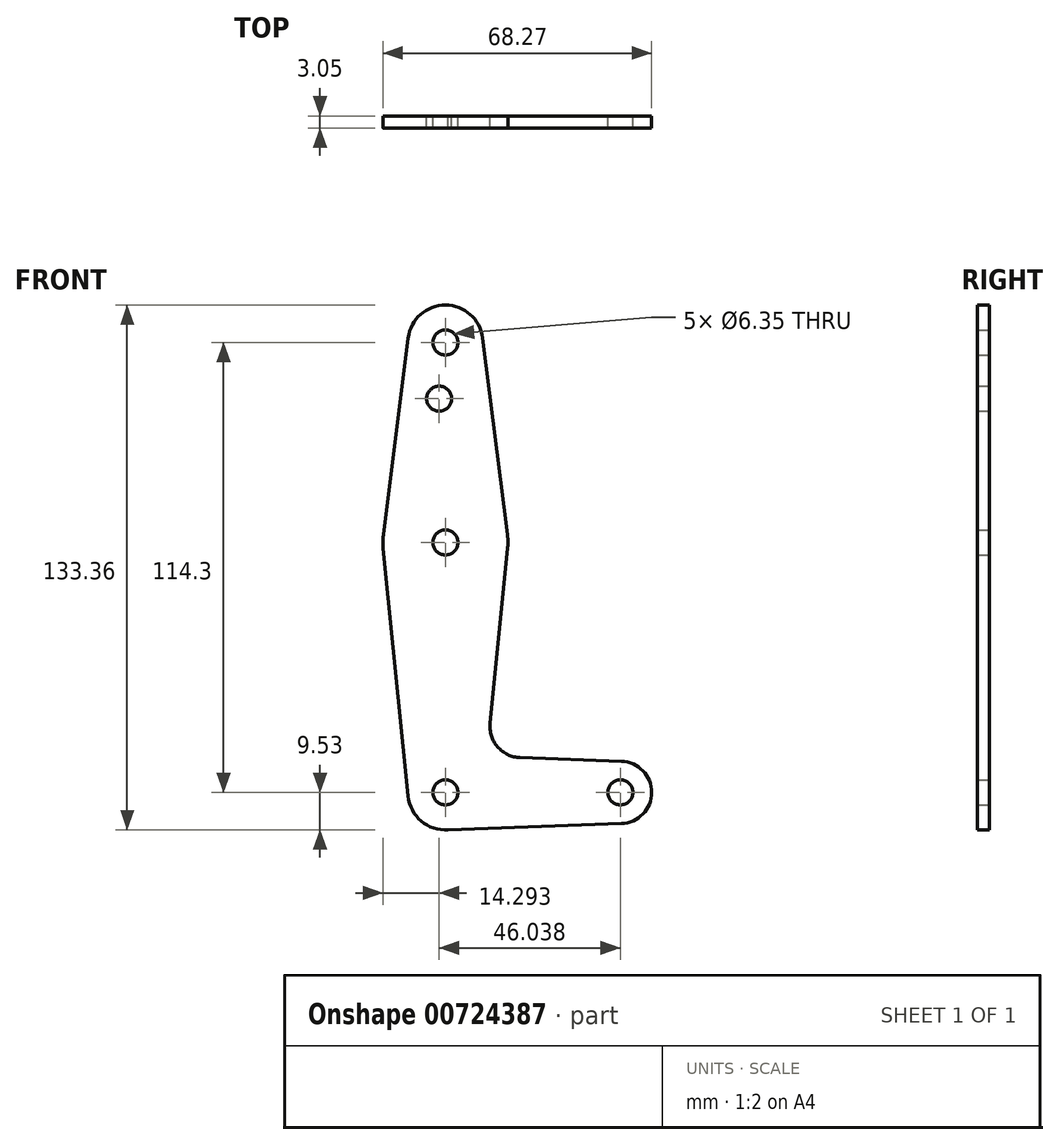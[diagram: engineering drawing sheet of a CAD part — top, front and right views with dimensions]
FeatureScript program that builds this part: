
annotation { "Feature Type Name" : "Feature", "Feature Type Description" : "" }
export const myFeature = defineFeature(function(context is Context, id is Id, definition is map)
    precondition{}
    {
        {
            var Q0;
            Q0=qCreatedBy(makeId("Front.planeOp"),FACE);
            var sketch = newSketch(context, id + "F0", { "sketchPlane" : qUnion([Q0])});
            skLineSegment(sketch, "E0", {"start": v(0, 114.3) * mm, "end": v(0, 0) * mm, "construction": true});
            skLineSegment(sketch, "E1", {"start": v(0, 0) * mm, "end": v(44.45, 0) * mm, "construction": true});
            skCircle(sketch, "E2", {"center": v(0, 0) * mm, "radius": 9.53 * mm});
            skCircle(sketch, "E3", {"center": v(0, 114.3) * mm, "radius": 9.53 * mm});
            skCircle(sketch, "E4", {"center": v(44.45, 0) * mm, "radius": 7.94 * mm});
            skCircle(sketch, "E5", {"center": v(0, 63.5) * mm, "radius": 15.88 * mm});
            skLineSegment(sketch, "E6", {"start": v(-9.45, 115.5) * mm, "end": v(-15.75, 65.48) * mm});
            skLineSegment(sketch, "E7", {"start": v(9.45, 115.5) * mm, "end": v(15.75, 65.48) * mm});
            skLineSegment(sketch, "E8", {"start": v(-15.8, 61.91) * mm, "end": v(-9.48, -0.95) * mm});
            skLineSegment(sketch, "E9", {"start": v(15.8, 61.91) * mm, "end": v(11.34, 17.59) * mm});
            skLineSegment(sketch, "E10", {"start": v(18.97, 8.85) * mm, "end": v(44.73, 7.93) * mm});
            skLineSegment(sketch, "E11", {"start": v(0, -9.53) * mm, "end": v(44.73, -7.93) * mm});
            skCircle(sketch, "E12", {"center": v(0, 114.3) * mm, "radius": 3.18 * mm});
            skCircle(sketch, "E13", {"center": v(-1.59, 100.03) * mm, "radius": 3.18 * mm});
            skCircle(sketch, "E14", {"center": v(0, 63.5) * mm, "radius": 3.18 * mm});
            skCircle(sketch, "E15", {"center": v(0, 0) * mm, "radius": 3.18 * mm});
            skCircle(sketch, "E16", {"center": v(44.45, 0) * mm, "radius": 3.18 * mm});
            skPoint(sketch, "E17.newPointA", {"position": v(9.48, -0.95) * mm});
            skArc(sketch, "E17.filletArc", {"start": v(11.34, 17.59) * mm, "mid": v(13.26, 11.57) * mm, "end": v(18.97, 8.85) * mm});
            skSolve(sketch);
        }
        {
            var Q0;
            Q0 = qSketchRegion(id + "F0", true);
            extrude(context, id + "F1", {"entities" : qUnion([Q0]), "depth" : 3.05 * mm, "offsetDistance" : 25.4 * mm});
        }
    });
